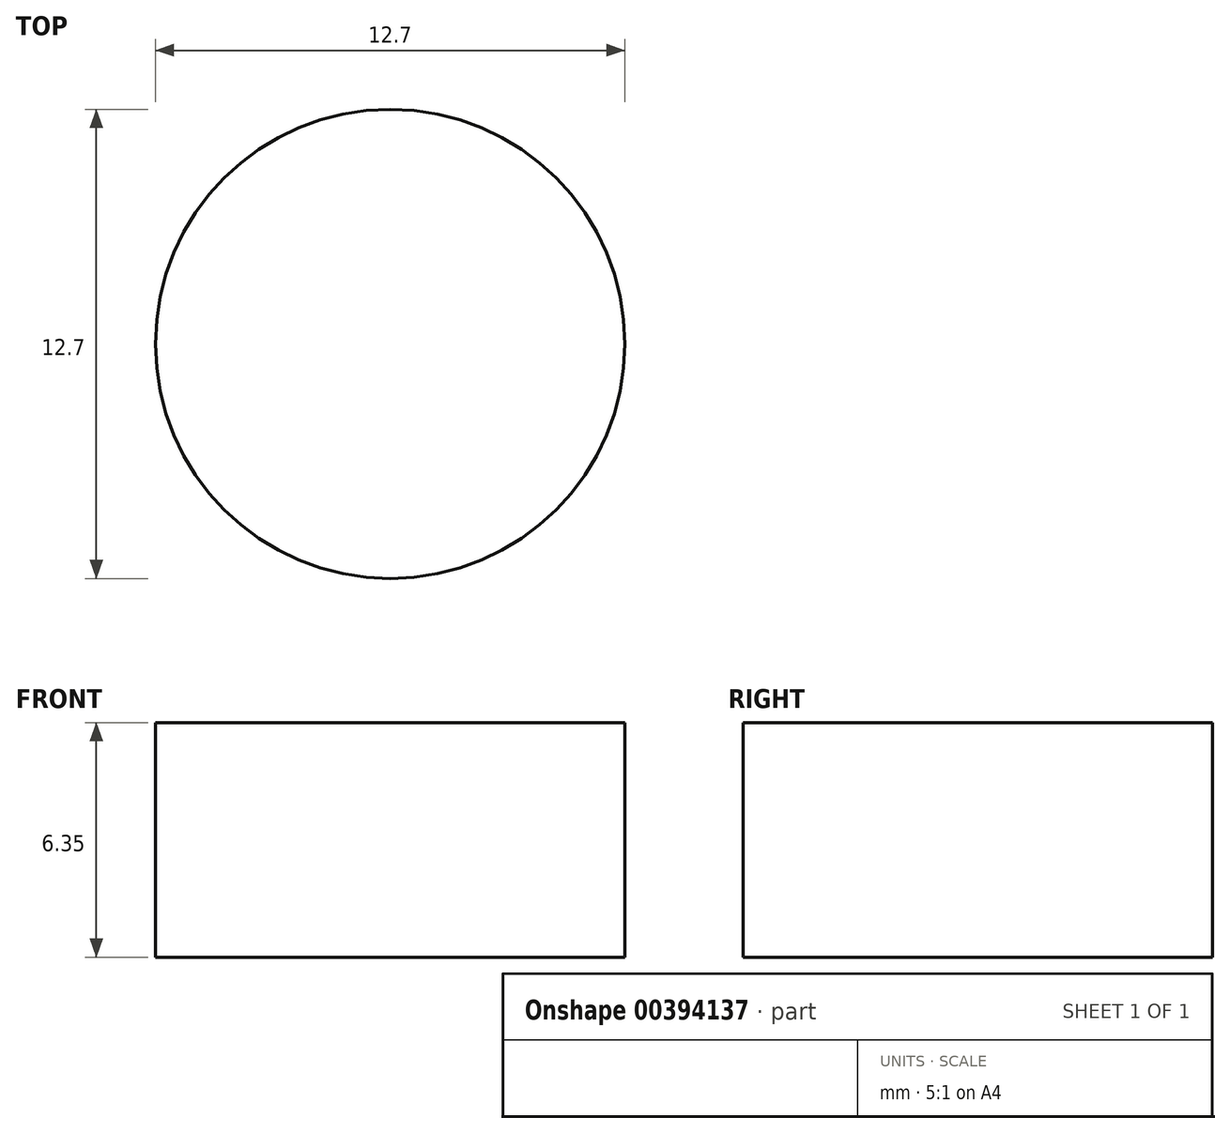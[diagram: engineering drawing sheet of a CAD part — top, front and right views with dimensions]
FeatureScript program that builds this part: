
annotation { "Feature Type Name" : "Feature", "Feature Type Description" : "" }
export const myFeature = defineFeature(function(context is Context, id is Id, definition is map)
    precondition{}
    {
        {
            var Q0;
            Q0=qCreatedBy(makeId("Top.planeOp"),FACE);
            var sketch = newSketch(context, id + "F0", { "sketchPlane" : qUnion([Q0])});
            skPoint(sketch, "E0.visualSharp", {"position": v(-79.2, -25) * mm});
            skLineSegment(sketch, "E1.bottom", {"start": v(-63.5, 22.22) * mm, "end": v(63.5, 22.23) * mm});
            skLineSegment(sketch, "E1.top", {"start": v(-63.5, -22.23) * mm, "end": v(63.5, -22.22) * mm});
            skLineSegment(sketch, "E1.left", {"start": v(-63.5, 22.22) * mm, "end": v(-63.5, -22.23) * mm});
            skLineSegment(sketch, "E1.right", {"start": v(63.5, 22.23) * mm, "end": v(63.5, -22.22) * mm});
            skSolve(sketch);
        }
        {
            var Q0;
            Q0=makeQuery(id+"F0.imprint","IMPRINT",FACE,{"disambiguationData":[TD([[makeQuery(id+"F0.imprint","IMPRINT",EDGE,{"derivedFrom":sQuery(id+"F0.wireOp",EDGE,"E1.bottom")}),-1.0]])]});
            extrude(context, id + "F1", {"entities" : qUnion([Q0]), "depth" : 6.35 * mm});
        }
        {
            var Q0;
            Q0=makeQuery(id+"F1.opExtrude","SWEPT_EDGE",EDGE,{"disambiguationData":[OSD([sQuery(id+"F0.wireOp",EDGE,"E1.top"),sQuery(id+"F0.wireOp",EDGE,"E1.right")])]});
            var Q1;
            Q1=makeQuery(id+"F1.opExtrude","SWEPT_EDGE",EDGE,{"disambiguationData":[OSD([sQuery(id+"F0.wireOp",EDGE,"E1.bottom"),sQuery(id+"F0.wireOp",EDGE,"E1.right")])]});
            var Q2;
            Q2=makeQuery(id+"F1.opExtrude","SWEPT_EDGE",EDGE,{"disambiguationData":[OSD([sQuery(id+"F0.wireOp",EDGE,"E1.top"),sQuery(id+"F0.wireOp",EDGE,"E1.left")])]});
            var Q3;
            Q3=makeQuery(id+"F1.opExtrude","SWEPT_EDGE",EDGE,{"disambiguationData":[OSD([sQuery(id+"F0.wireOp",EDGE,"E1.bottom"),sQuery(id+"F0.wireOp",EDGE,"E1.left")])]});
            fillet(context, id + "F2", {"entities" : qUnion([Q0, Q1, Q2, Q3]), "radius" : 5.08 * mm, "tangentPropagation" : true, "allowEdgeOverflow" : false});
        }
        {
            var Q0;
            Q0=makeQuery(id+"F1.opExtrude","CAP_FACE",FACE,{"disambiguationData":[OSD([sQuery(id+"F0.wireOp",EDGE,"E1.bottom"),sQuery(id+"F0.wireOp",EDGE,"E1.top"),sQuery(id+"F0.wireOp",EDGE,"E1.left"),sQuery(id+"F0.wireOp",EDGE,"E1.right")])],"isStart":false});
            var sketch = newSketch(context, id + "F3", { "sketchPlane" : qUnion([Q0])});
            skCircle(sketch, "E2", {"center": v(-44.45, 0) * mm, "radius": 6.35 * mm});
            skCircle(sketch, "E3.MirrorC", {"center": v(44.45, 0) * mm, "radius": 6.35 * mm});
            skSolve(sketch);
        }
        {
            var Q0;
            Q0=makeQuery(id+"F3.imprint","IMPRINT",FACE,{"disambiguationData":[TD([[makeQuery(id+"F3.imprint","IMPRINT",EDGE,{"derivedFrom":sQuery(id+"F3.wireOp",EDGE,"E2")}),1.0]])]});
            var Q1;
            Q1=makeQuery(id+"F3.imprint","IMPRINT",FACE,{"disambiguationData":[TD([[makeQuery(id+"F3.imprint","IMPRINT",EDGE,{"derivedFrom":sQuery(id+"F3.wireOp",EDGE,"E3.MirrorC")}),-1.0]])]});
            var Q2;
            Q2=makeQuery(id+"F1.opExtrude","CAP_FACE",FACE,{"disambiguationData":[OSD([sQuery(id+"F0.wireOp",EDGE,"E1.bottom"),sQuery(id+"F0.wireOp",EDGE,"E1.top"),sQuery(id+"F0.wireOp",EDGE,"E1.left"),sQuery(id+"F0.wireOp",EDGE,"E1.right")])],"isStart":true});
            extrude(context, id + "F4", {"entities" : qUnion([Q0, Q1]), "operationType" : NewBodyOperationType.REMOVE, "endBound" : BoundingType.UP_TO_SURFACE, "oppositeDirection" : true, "endBoundEntityFace" : qUnion([Q2]), "depth" : 12.7 * mm});
        }
    });
